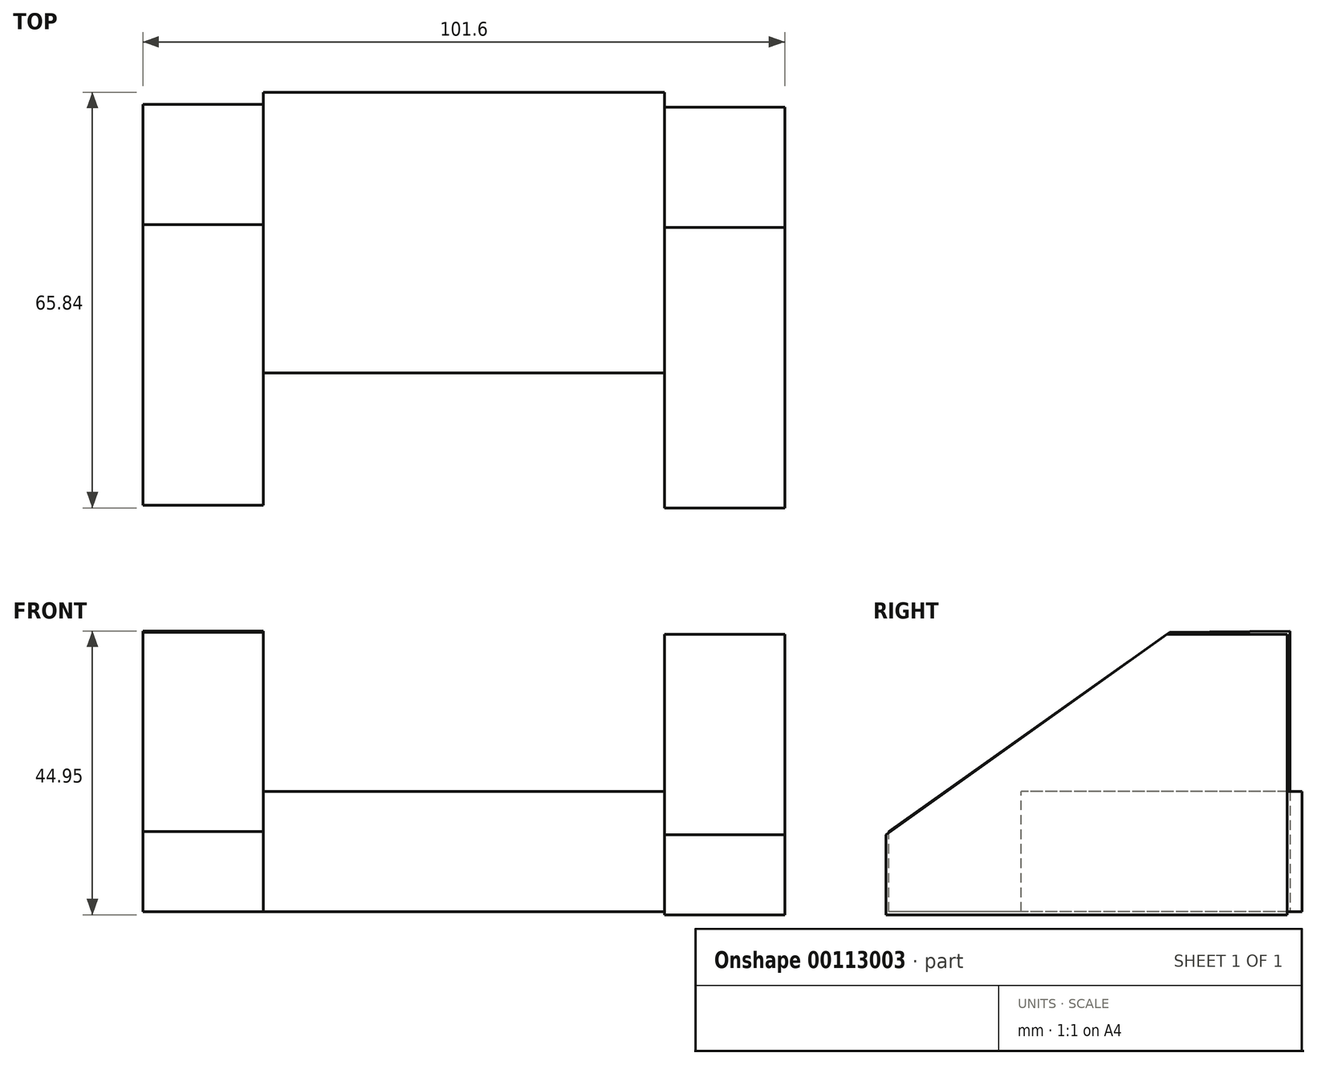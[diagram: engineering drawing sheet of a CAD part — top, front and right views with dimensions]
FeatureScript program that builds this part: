
annotation { "Feature Type Name" : "Feature", "Feature Type Description" : "" }
export const myFeature = defineFeature(function(context is Context, id is Id, definition is map)
    precondition{}
    {
        {
            var Q0;
            Q0=qCreatedBy(makeId("Right.planeOp"),FACE);
            var sketch = newSketch(context, id + "F0", { "sketchPlane" : qUnion([Q0])});
            skLineSegment(sketch, "E0", {"start": v(23.06, 52.5) * mm, "end": v(42.11, 52.5) * mm});
            skLineSegment(sketch, "E1", {"start": v(42.11, 52.5) * mm, "end": v(42.11, 8.05) * mm});
            skLineSegment(sketch, "E2", {"start": v(42.11, 8.05) * mm, "end": v(-21.39, 8.05) * mm});
            skLineSegment(sketch, "E3", {"start": v(-21.39, 8.05) * mm, "end": v(-21.39, 20.75) * mm});
            skLineSegment(sketch, "E4", {"start": v(-21.39, 20.75) * mm, "end": v(23.06, 52.5) * mm});
            skSolve(sketch);
        }
        {
            var Q0;
            Q0=makeQuery(id+"F0.imprint","IMPRINT",FACE,{"disambiguationData":[TD([[makeQuery(id+"F0.imprint","IMPRINT",EDGE,{"derivedFrom":sQuery(id+"F0.wireOp",EDGE,"E0")}),-1.0]])]});
            var sketch = newSketch(context, id + "F1", { "sketchPlane" : qUnion([Q0])});
            skLineSegment(sketch, "E5.bottom", {"start": v(44.45, 8.55) * mm, "end": v(0, 8.55) * mm});
            skLineSegment(sketch, "E5.top", {"start": v(44.45, 27.6) * mm, "end": v(0, 27.6) * mm});
            skLineSegment(sketch, "E5.left", {"start": v(44.45, 8.55) * mm, "end": v(44.45, 27.6) * mm});
            skLineSegment(sketch, "E5.right", {"start": v(0, 8.55) * mm, "end": v(0, 27.6) * mm});
            skSolve(sketch);
        }
        {
            var Q0;
            Q0 = qSketchRegion(id + "F1", true);
            extrude(context, id + "F2", {"entities" : qUnion([Q0]), "oppositeDirection" : true, "depth" : 63.5 * mm});
        }
        {
            var Q0;
            Q0=makeQuery(id+"F0.imprint","IMPRINT",FACE,{"disambiguationData":[TD([[makeQuery(id+"F0.imprint","IMPRINT",EDGE,{"derivedFrom":sQuery(id+"F0.wireOp",EDGE,"E0")}),-1.0]])]});
            extrude(context, id + "F3", {"entities" : qUnion([Q0]), "operationType" : NewBodyOperationType.ADD, "depth" : 19.05 * mm});
        }
        {
            var Q0;
            Q0=makeQuery(id+"F2.opExtrude","CAP_FACE",FACE,{"disambiguationData":[OSD([sQuery(id+"F1.wireOp",EDGE,"E5.bottom"),sQuery(id+"F1.wireOp",EDGE,"E5.top"),sQuery(id+"F1.wireOp",EDGE,"E5.left"),sQuery(id+"F1.wireOp",EDGE,"E5.right")])],"isStart":false});
            var sketch = newSketch(context, id + "F4", { "sketchPlane" : qUnion([Q0])});
            skLineSegment(sketch, "E6", {"start": v(-42.55, 53) * mm, "end": v(-42.55, 8.55) * mm});
            skLineSegment(sketch, "E7", {"start": v(-42.55, 8.55) * mm, "end": v(20.95, 8.55) * mm});
            skLineSegment(sketch, "E8", {"start": v(20.95, 8.55) * mm, "end": v(20.95, 21.25) * mm});
            skLineSegment(sketch, "E9", {"start": v(20.95, 21.25) * mm, "end": v(-23.5, 52.79) * mm});
            skLineSegment(sketch, "E10", {"start": v(-23.5, 52.79) * mm, "end": v(-42.55, 53) * mm});
            skSolve(sketch);
        }
        {
            var Q0;
            Q0 = qSketchRegion(id + "F4", true);
            extrude(context, id + "F5", {"entities" : qUnion([Q0]), "operationType" : NewBodyOperationType.ADD, "depth" : 19.05 * mm});
        }
    });
